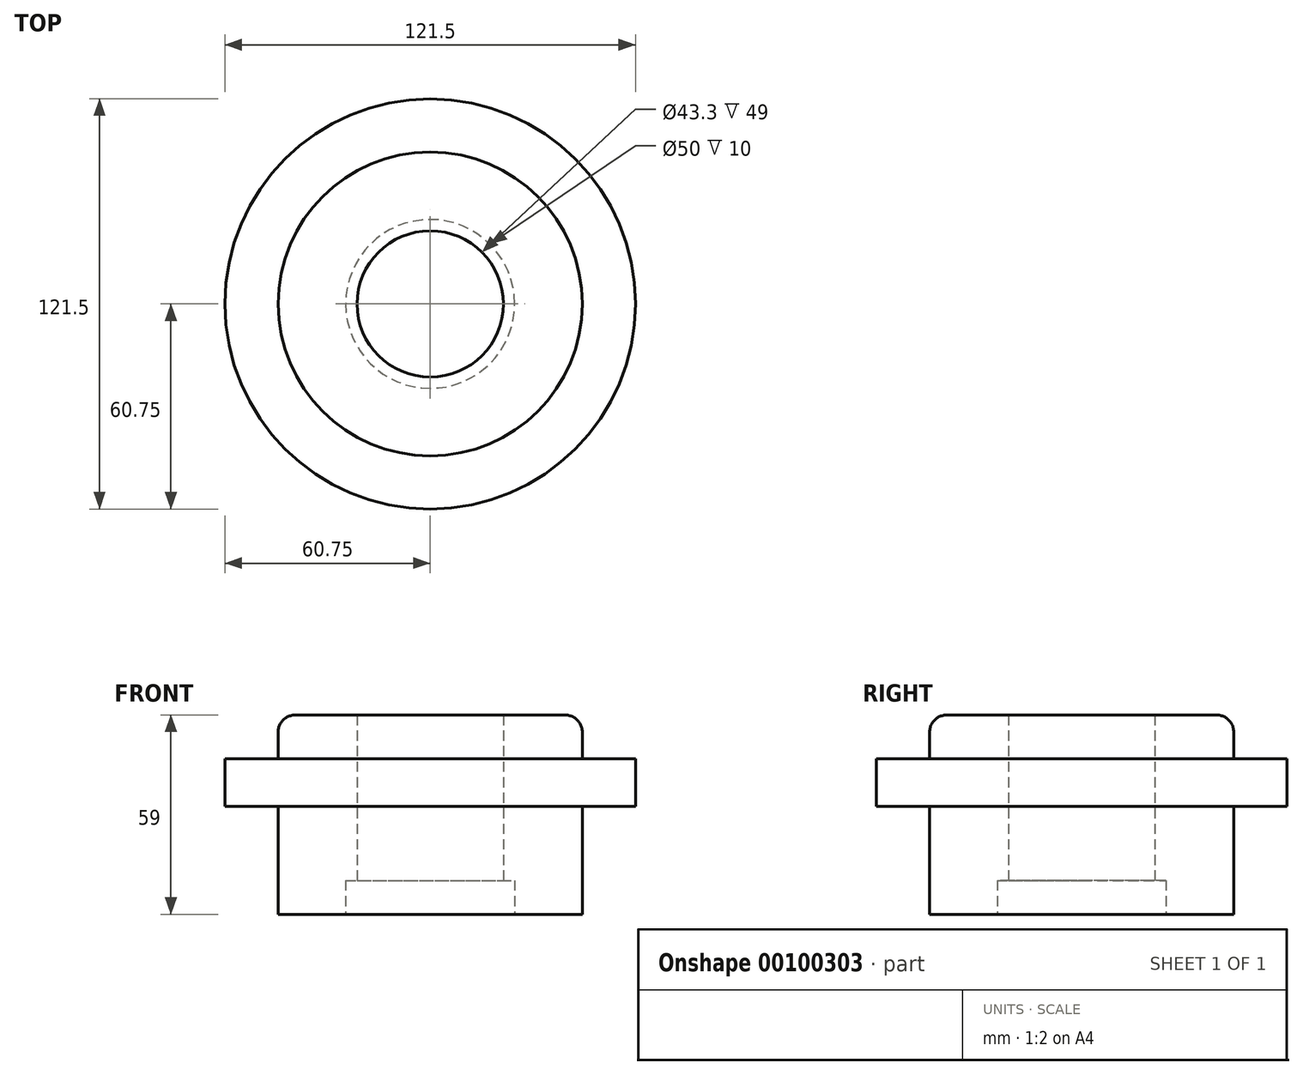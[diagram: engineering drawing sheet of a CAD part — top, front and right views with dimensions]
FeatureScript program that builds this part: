
annotation { "Feature Type Name" : "Feature", "Feature Type Description" : "" }
export const myFeature = defineFeature(function(context is Context, id is Id, definition is map)
    precondition{}
    {
        {
            var Q0;
            Q0=qCreatedBy(makeId("Front.planeOp"),FACE);
            var sketch = newSketch(context, id + "F0", { "sketchPlane" : qUnion([Q0])});
            skLineSegment(sketch, "E0", {"start": v(-60.75, 0) * mm, "end": v(-60.75, 14) * mm});
            skLineSegment(sketch, "E1", {"start": v(-60.75, 14) * mm, "end": v(-45, 14) * mm});
            skLineSegment(sketch, "E2", {"start": v(-45, 14) * mm, "end": v(-45, 27) * mm});
            skLineSegment(sketch, "E3", {"start": v(-45, 27) * mm, "end": v(-21.65, 27) * mm});
            skLineSegment(sketch, "E4", {"start": v(-21.65, 27) * mm, "end": v(-21.65, -32) * mm});
            skLineSegment(sketch, "E5", {"start": v(-21.65, -32) * mm, "end": v(-45, -32) * mm});
            skLineSegment(sketch, "E6", {"start": v(-45, -32) * mm, "end": v(-45, 0) * mm});
            skLineSegment(sketch, "E7", {"start": v(-45, 0) * mm, "end": v(-60.75, 0) * mm});
            skLineSegment(sketch, "E8", {"start": v(0, 0) * mm, "end": v(0, 56.62) * mm, "construction": true});
            skSolve(sketch);
        }
        {
            var Q0;
            Q0=makeQuery(id+"F0.imprint","IMPRINT",FACE,{"disambiguationData":[TD([[makeQuery(id+"F0.imprint","IMPRINT",EDGE,{"derivedFrom":sQuery(id+"F0.wireOp",EDGE,"E0")}),-1.0]])]});
            var Q1;
            Q1=sQuery(id+"F0.wireOp",EDGE,"E8");
            revolve(context, id + "F1", {"entities" : qUnion([Q0]), "axis" : qUnion([Q1]), "revolveType" : RevolveType.FULL});
        }
        {
            var Q0;
            Q0=makeQuery(id+"F1.opRevolve","SWEPT_EDGE",EDGE,{"disambiguationData":[OSD([sQuery(id+"F0.wireOp",EDGE,"E2"),sQuery(id+"F0.wireOp",EDGE,"E3")])]});
            fillet(context, id + "F2", {"entities" : qUnion([Q0]), "radius" : 5 * mm, "tangentPropagation" : true, "allowEdgeOverflow" : false});
        }
        {
            var Q0;
            Q0=makeQuery(id+"F1.opRevolve","SWEPT_FACE",FACE,{"disambiguationData":[OSD([sQuery(id+"F0.wireOp",EDGE,"E5")])]});
            var sketch = newSketch(context, id + "F3", { "sketchPlane" : qUnion([Q0])});
            skCircle(sketch, "E9", {"center": v(0, 0) * mm, "radius": 25 * mm});
            skSolve(sketch);
        }
        {
            var Q0;
            Q0=qSketchRegion(id+"F3",true);
            extrude(context, id + "F4", {"entities" : qUnion([Q0]), "operationType" : NewBodyOperationType.REMOVE, "oppositeDirection" : true, "depth" : 10 * mm});
        }
    });
